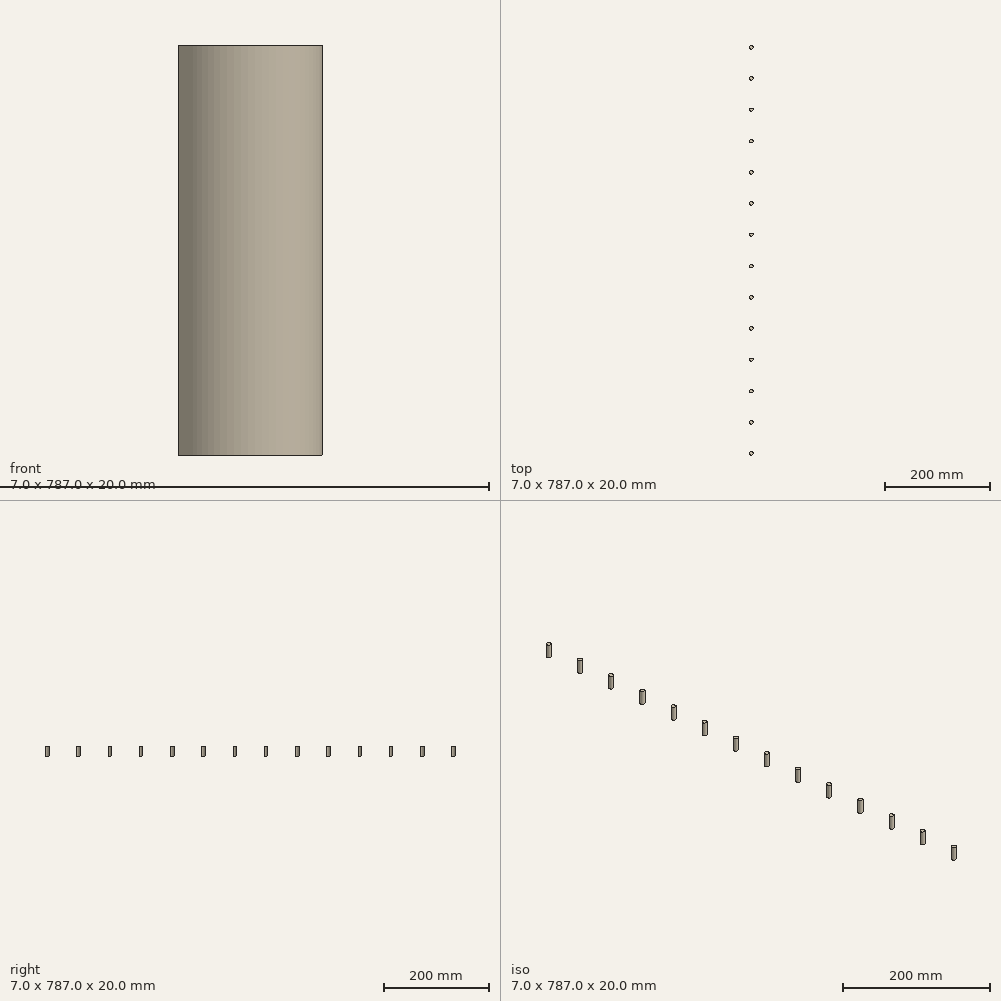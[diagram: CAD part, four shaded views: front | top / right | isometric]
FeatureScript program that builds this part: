
annotation { "Feature Type Name" : "Feature", "Feature Type Description" : "" }
export const myFeature = defineFeature(function(context is Context, id is Id, definition is map)
    precondition{}
    {
        {
            var Q0;
            Q0=qCreatedBy(makeId("Front.planeOp"),FACE);
            var sketch = newSketch(context, id + "F0", { "sketchPlane" : qUnion([Q0])});
            skLineSegment(sketch, "E0.bottom", {"start": v(50, 10) * mm, "end": v(-50, 10) * mm});
            skLineSegment(sketch, "E0.top", {"start": v(50, -10) * mm, "end": v(-50, -10) * mm});
            skLineSegment(sketch, "E0.left", {"start": v(50, 10) * mm, "end": v(50, -10) * mm});
            skLineSegment(sketch, "E0.right", {"start": v(-50, 10) * mm, "end": v(-50, -10) * mm});
            skPoint(sketch, "E0.middle", {"position": v(0, 0) * mm});
            skSolve(sketch);
        }
        {
            var Q0;
            Q0=makeQuery(id+"F0.imprint","IMPRINT",FACE,{"disambiguationData":[TD([[makeQuery(id+"F0.imprint","IMPRINT",EDGE,{"derivedFrom":sQuery(id+"F0.wireOp",EDGE,"E0.bottom")}),1.0]])]});
            extrude(context, id + "F1", {"entities" : qUnion([Q0]), "oppositeDirection" : true, "depth" : 900 * mm});
        }
        {
            var Q0;
            Q0=makeQuery(id+"F1.opExtrude","SWEPT_FACE",FACE,{"disambiguationData":[OSD([sQuery(id+"F0.wireOp",EDGE,"E0.bottom")])]});
            var sketch = newSketch(context, id + "F2", { "sketchPlane" : qUnion([Q0])});
            skCircle(sketch, "E1", {"center": v(-40, 60) * mm, "radius": 3.5 * mm});
            skCircle(sketch, "E2.0.1.0", {"center": v(-40, 120) * mm, "radius": 3.5 * mm});
            skCircle(sketch, "E2.0.2.0", {"center": v(-40, 180) * mm, "radius": 3.5 * mm});
            skCircle(sketch, "E2.0.3.0", {"center": v(-40, 240) * mm, "radius": 3.5 * mm});
            skCircle(sketch, "E2.0.4.0", {"center": v(-40, 300) * mm, "radius": 3.5 * mm});
            skCircle(sketch, "E2.0.5.0", {"center": v(-40, 360) * mm, "radius": 3.5 * mm});
            skCircle(sketch, "E2.0.6.0", {"center": v(-40, 420) * mm, "radius": 3.5 * mm});
            skCircle(sketch, "E2.0.7.0", {"center": v(-40, 480) * mm, "radius": 3.5 * mm});
            skCircle(sketch, "E2.0.8.0", {"center": v(-40, 540) * mm, "radius": 3.5 * mm});
            skCircle(sketch, "E2.0.9.0", {"center": v(-40, 600) * mm, "radius": 3.5 * mm});
            skCircle(sketch, "E2.0.10.0", {"center": v(-40, 660) * mm, "radius": 3.5 * mm});
            skCircle(sketch, "E2.0.11.0", {"center": v(-40, 720) * mm, "radius": 3.5 * mm});
            skLineSegment(sketch, "E2.direction1", {"start": v(-40, 60) * mm, "end": v(-15, 60) * mm, "construction": true});
            skLineSegment(sketch, "E2.direction2", {"start": v(-40, 60) * mm, "end": v(-40, 120) * mm, "construction": true});
            skCircle(sketch, "E3.0.0.12", {"center": v(-40, 780) * mm, "radius": 3.5 * mm});
            skCircle(sketch, "E3.0.0.13", {"center": v(-40, 840) * mm, "radius": 3.5 * mm});
            skLineSegment(sketch, "E4", {"start": v(0, 900) * mm, "end": v(0, 0) * mm, "construction": true});
            skCircle(sketch, "E5.MirrorC", {"center": v(40, 60) * mm, "radius": 3.5 * mm});
            skCircle(sketch, "E6.MirrorC", {"center": v(40, 120) * mm, "radius": 3.5 * mm});
            skCircle(sketch, "E7.MirrorC", {"center": v(40, 420) * mm, "radius": 3.5 * mm});
            skCircle(sketch, "E8.MirrorC", {"center": v(40, 360) * mm, "radius": 3.5 * mm});
            skCircle(sketch, "E9.MirrorC", {"center": v(40, 300) * mm, "radius": 3.5 * mm});
            skCircle(sketch, "E10.MirrorC", {"center": v(40, 480) * mm, "radius": 3.5 * mm});
            skCircle(sketch, "E11.MirrorC", {"center": v(40, 540) * mm, "radius": 3.5 * mm});
            skCircle(sketch, "E12.MirrorC", {"center": v(40, 600) * mm, "radius": 3.5 * mm});
            skCircle(sketch, "E13.MirrorC", {"center": v(40, 660) * mm, "radius": 3.5 * mm});
            skCircle(sketch, "E14.MirrorC", {"center": v(40, 720) * mm, "radius": 3.5 * mm});
            skCircle(sketch, "E15.MirrorC", {"center": v(40, 780) * mm, "radius": 3.5 * mm});
            skCircle(sketch, "E16.MirrorC", {"center": v(40, 840) * mm, "radius": 3.5 * mm});
            skCircle(sketch, "E17.MirrorC", {"center": v(40, 180) * mm, "radius": 3.5 * mm});
            skCircle(sketch, "E18.MirrorC", {"center": v(40, 240) * mm, "radius": 3.5 * mm});
            skLineSegment(sketch, "E19.MirrorCS", {"start": v(40, 60) * mm, "end": v(40, 120) * mm, "construction": true});
            skSolve(sketch);
        }
        {
            var Q0;
            Q0=makeQuery(id+"F2.imprint","IMPRINT",FACE,{"disambiguationData":[TD([[makeQuery(id+"F2.imprint","IMPRINT",EDGE,{"derivedFrom":sQuery(id+"F2.wireOp",EDGE,"E1")}),1.0]])]});
            var Q1;
            Q1=makeQuery(id+"F2.imprint","IMPRINT",FACE,{"disambiguationData":[TD([[makeQuery(id+"F2.imprint","IMPRINT",EDGE,{"derivedFrom":sQuery(id+"F2.wireOp",EDGE,"E5.MirrorC")}),-1.0]])]});
            var Q2;
            Q2=makeQuery(id+"F2.imprint","IMPRINT",FACE,{"disambiguationData":[TD([[makeQuery(id+"F2.imprint","IMPRINT",EDGE,{"derivedFrom":sQuery(id+"F2.wireOp",EDGE,"E6.MirrorC")}),-1.0]])]});
            var Q3;
            Q3=makeQuery(id+"F2.imprint","IMPRINT",FACE,{"disambiguationData":[TD([[makeQuery(id+"F2.imprint","IMPRINT",EDGE,{"derivedFrom":sQuery(id+"F2.wireOp",EDGE,"E2.0.1.0")}),1.0]])]});
            var Q4;
            Q4=makeQuery(id+"F2.imprint","IMPRINT",FACE,{"disambiguationData":[TD([[makeQuery(id+"F2.imprint","IMPRINT",EDGE,{"derivedFrom":sQuery(id+"F2.wireOp",EDGE,"E2.0.2.0")}),1.0]])]});
            var Q5;
            Q5=makeQuery(id+"F2.imprint","IMPRINT",FACE,{"disambiguationData":[TD([[makeQuery(id+"F2.imprint","IMPRINT",EDGE,{"derivedFrom":sQuery(id+"F2.wireOp",EDGE,"E17.MirrorC")}),-1.0]])]});
            var Q6;
            Q6=makeQuery(id+"F2.imprint","IMPRINT",FACE,{"disambiguationData":[TD([[makeQuery(id+"F2.imprint","IMPRINT",EDGE,{"derivedFrom":sQuery(id+"F2.wireOp",EDGE,"E18.MirrorC")}),-1.0]])]});
            var Q7;
            Q7=makeQuery(id+"F2.imprint","IMPRINT",FACE,{"disambiguationData":[TD([[makeQuery(id+"F2.imprint","IMPRINT",EDGE,{"derivedFrom":sQuery(id+"F2.wireOp",EDGE,"E2.0.3.0")}),1.0]])]});
            var Q8;
            Q8=makeQuery(id+"F2.imprint","IMPRINT",FACE,{"disambiguationData":[TD([[makeQuery(id+"F2.imprint","IMPRINT",EDGE,{"derivedFrom":sQuery(id+"F2.wireOp",EDGE,"E9.MirrorC")}),-1.0]])]});
            var Q9;
            Q9=makeQuery(id+"F2.imprint","IMPRINT",FACE,{"disambiguationData":[TD([[makeQuery(id+"F2.imprint","IMPRINT",EDGE,{"derivedFrom":sQuery(id+"F2.wireOp",EDGE,"E2.0.4.0")}),1.0]])]});
            var Q10;
            Q10=makeQuery(id+"F2.imprint","IMPRINT",FACE,{"disambiguationData":[TD([[makeQuery(id+"F2.imprint","IMPRINT",EDGE,{"derivedFrom":sQuery(id+"F2.wireOp",EDGE,"E2.0.5.0")}),1.0]])]});
            var Q11;
            Q11=makeQuery(id+"F2.imprint","IMPRINT",FACE,{"disambiguationData":[TD([[makeQuery(id+"F2.imprint","IMPRINT",EDGE,{"derivedFrom":sQuery(id+"F2.wireOp",EDGE,"E8.MirrorC")}),-1.0]])]});
            var Q12;
            Q12=makeQuery(id+"F2.imprint","IMPRINT",FACE,{"disambiguationData":[TD([[makeQuery(id+"F2.imprint","IMPRINT",EDGE,{"derivedFrom":sQuery(id+"F2.wireOp",EDGE,"E7.MirrorC")}),-1.0]])]});
            var Q13;
            Q13=makeQuery(id+"F2.imprint","IMPRINT",FACE,{"disambiguationData":[TD([[makeQuery(id+"F2.imprint","IMPRINT",EDGE,{"derivedFrom":sQuery(id+"F2.wireOp",EDGE,"E2.0.6.0")}),1.0]])]});
            var Q14;
            Q14=makeQuery(id+"F2.imprint","IMPRINT",FACE,{"disambiguationData":[TD([[makeQuery(id+"F2.imprint","IMPRINT",EDGE,{"derivedFrom":sQuery(id+"F2.wireOp",EDGE,"E10.MirrorC")}),-1.0]])]});
            var Q15;
            Q15=makeQuery(id+"F2.imprint","IMPRINT",FACE,{"disambiguationData":[TD([[makeQuery(id+"F2.imprint","IMPRINT",EDGE,{"derivedFrom":sQuery(id+"F2.wireOp",EDGE,"E11.MirrorC")}),-1.0]])]});
            var Q16;
            Q16=makeQuery(id+"F2.imprint","IMPRINT",FACE,{"disambiguationData":[TD([[makeQuery(id+"F2.imprint","IMPRINT",EDGE,{"derivedFrom":sQuery(id+"F2.wireOp",EDGE,"E12.MirrorC")}),-1.0]])]});
            var Q17;
            Q17=makeQuery(id+"F2.imprint","IMPRINT",FACE,{"disambiguationData":[TD([[makeQuery(id+"F2.imprint","IMPRINT",EDGE,{"derivedFrom":sQuery(id+"F2.wireOp",EDGE,"E2.0.9.0")}),1.0]])]});
            var Q18;
            Q18=makeQuery(id+"F2.imprint","IMPRINT",FACE,{"disambiguationData":[TD([[makeQuery(id+"F2.imprint","IMPRINT",EDGE,{"derivedFrom":sQuery(id+"F2.wireOp",EDGE,"E2.0.8.0")}),1.0]])]});
            var Q19;
            Q19=makeQuery(id+"F2.imprint","IMPRINT",FACE,{"disambiguationData":[TD([[makeQuery(id+"F2.imprint","IMPRINT",EDGE,{"derivedFrom":sQuery(id+"F2.wireOp",EDGE,"E2.0.7.0")}),1.0]])]});
            var Q20;
            Q20=makeQuery(id+"F2.imprint","IMPRINT",FACE,{"disambiguationData":[TD([[makeQuery(id+"F2.imprint","IMPRINT",EDGE,{"derivedFrom":sQuery(id+"F2.wireOp",EDGE,"E13.MirrorC")}),-1.0]])]});
            var Q21;
            Q21=makeQuery(id+"F2.imprint","IMPRINT",FACE,{"disambiguationData":[TD([[makeQuery(id+"F2.imprint","IMPRINT",EDGE,{"derivedFrom":sQuery(id+"F2.wireOp",EDGE,"E2.0.10.0")}),1.0]])]});
            var Q22;
            Q22=makeQuery(id+"F2.imprint","IMPRINT",FACE,{"disambiguationData":[TD([[makeQuery(id+"F2.imprint","IMPRINT",EDGE,{"derivedFrom":sQuery(id+"F2.wireOp",EDGE,"E2.0.11.0")}),1.0]])]});
            var Q23;
            Q23=makeQuery(id+"F2.imprint","IMPRINT",FACE,{"disambiguationData":[TD([[makeQuery(id+"F2.imprint","IMPRINT",EDGE,{"derivedFrom":sQuery(id+"F2.wireOp",EDGE,"E14.MirrorC")}),-1.0]])]});
            var Q24;
            Q24=makeQuery(id+"F2.imprint","IMPRINT",FACE,{"disambiguationData":[TD([[makeQuery(id+"F2.imprint","IMPRINT",EDGE,{"derivedFrom":sQuery(id+"F2.wireOp",EDGE,"E15.MirrorC")}),-1.0]])]});
            var Q25;
            Q25=makeQuery(id+"F2.imprint","IMPRINT",FACE,{"disambiguationData":[TD([[makeQuery(id+"F2.imprint","IMPRINT",EDGE,{"derivedFrom":sQuery(id+"F2.wireOp",EDGE,"E3.0.0.12")}),1.0]])]});
            var Q26;
            Q26=makeQuery(id+"F2.imprint","IMPRINT",FACE,{"disambiguationData":[TD([[makeQuery(id+"F2.imprint","IMPRINT",EDGE,{"derivedFrom":sQuery(id+"F2.wireOp",EDGE,"E16.MirrorC")}),-1.0]])]});
            var Q27;
            Q27=makeQuery(id+"F2.imprint","IMPRINT",FACE,{"disambiguationData":[TD([[makeQuery(id+"F2.imprint","IMPRINT",EDGE,{"derivedFrom":sQuery(id+"F2.wireOp",EDGE,"E3.0.0.13")}),1.0]])]});
            extrude(context, id + "F3", {"entities" : qUnion([Q0, Q1, Q2, Q3, Q4, Q5, Q6, Q7, Q8, Q9, Q10, Q11, Q12, Q13, Q14, Q15, Q16, Q17, Q18, Q19, Q20, Q21, Q22, Q23, Q24, Q25, Q26, Q27]), "operationType" : NewBodyOperationType.REMOVE, "endBound" : BoundingType.UP_TO_NEXT, "oppositeDirection" : true, "depth" : 25 * mm, "offsetDistance" : 25 * mm});
        }
    });
